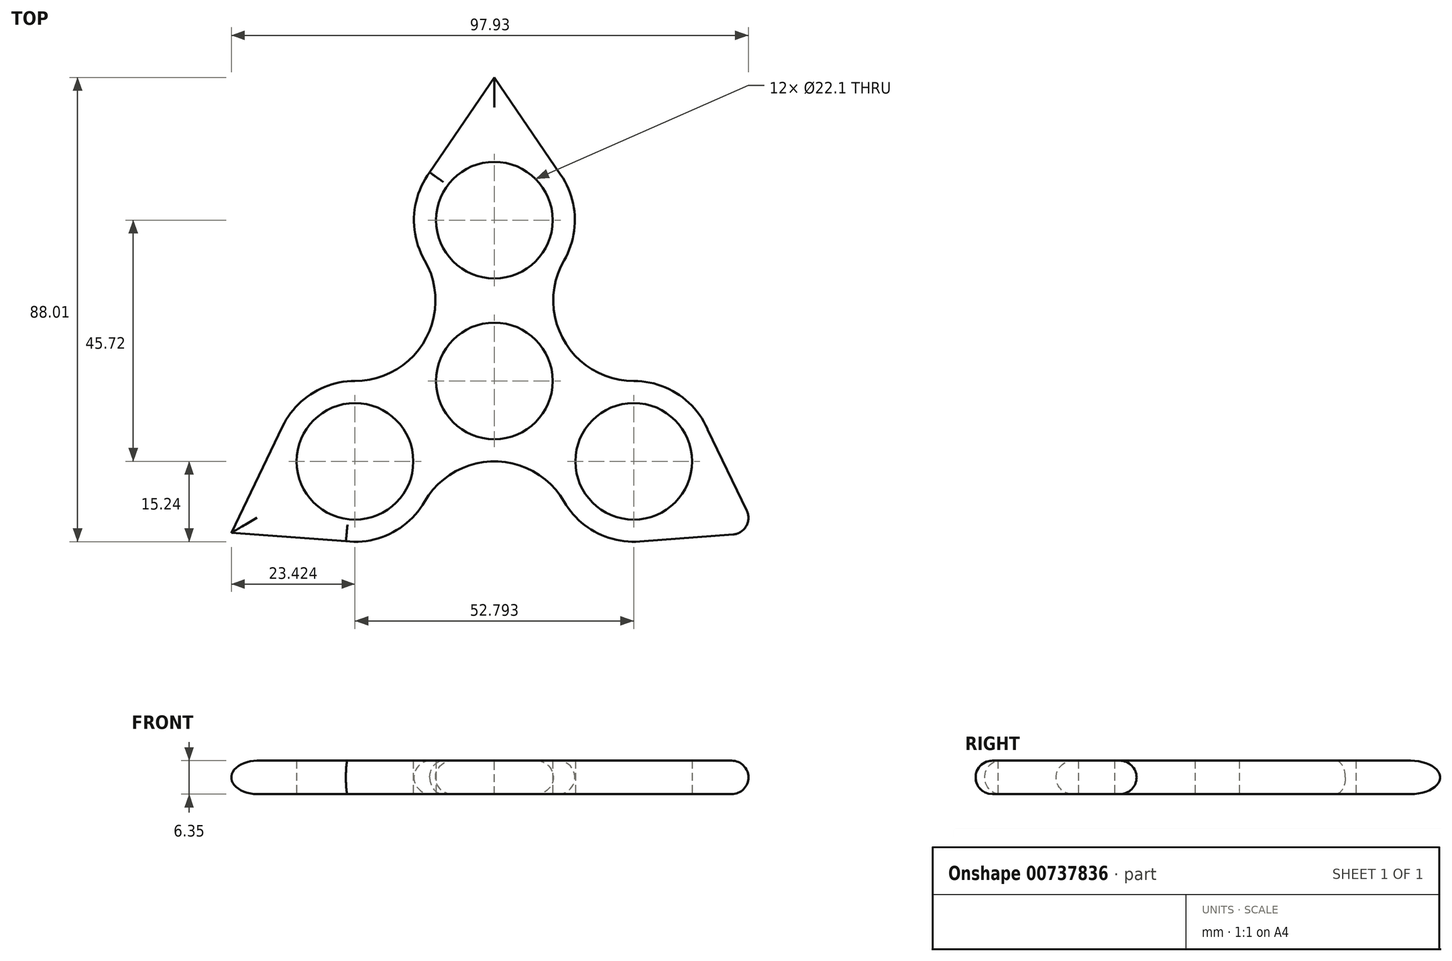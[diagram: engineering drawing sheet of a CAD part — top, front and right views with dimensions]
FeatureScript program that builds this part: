
annotation { "Feature Type Name" : "Feature", "Feature Type Description" : "" }
export const myFeature = defineFeature(function(context is Context, id is Id, definition is map)
    precondition{}
    {
        {
            var Q0;
            Q0=qCreatedBy(makeId("Top.planeOp"),FACE);
            var sketch = newSketch(context, id + "F0", { "sketchPlane" : qUnion([Q0])});
            skCircle(sketch, "E0", {"center": v(0, 0) * mm, "radius": 11.05 * mm});
            skLineSegment(sketch, "E1", {"start": v(0, 0) * mm, "end": v(0, 30.48) * mm});
            skArc(sketch, "E2", {"start": v(-12.25, 39.54) * mm, "mid": v(-15.22, 31.34) * mm, "end": v(-13.2, 22.86) * mm});
            skArc(sketch, "E3.1.0", {"start": v(-28.12, -30.38) * mm, "mid": v(-19.54, -28.85) * mm, "end": v(-13.2, -22.86) * mm});
            skArc(sketch, "E3.2.0", {"start": v(13.2, -22.86) * mm, "mid": v(19.28, -28.71) * mm, "end": v(27.54, -30.44) * mm});
            skLineSegment(sketch, "E4", {"start": v(0, 0) * mm, "end": v(-26.4, 15.24) * mm});
            skArc(sketch, "E5", {"start": v(-26.4, 0) * mm, "mid": v(-13.2, 7.62) * mm, "end": v(-13.2, 22.86) * mm});
            skArc(sketch, "E6.1.0", {"start": v(13.2, -22.86) * mm, "mid": v(0, -15.24) * mm, "end": v(-13.2, -22.86) * mm});
            skArc(sketch, "E6.2.0", {"start": v(13.2, 22.86) * mm, "mid": v(13.2, 7.62) * mm, "end": v(26.4, 0) * mm});
            skLineSegment(sketch, "E7", {"start": v(-12.25, 39.54) * mm, "end": v(0, 57.53) * mm});
            skLineSegment(sketch, "E8", {"start": v(0, 57.53) * mm, "end": v(12.6, 39.07) * mm});
            skLineSegment(sketch, "E9.1.0", {"start": v(-49.82, -28.76) * mm, "end": v(-40.13, -8.63) * mm});
            skLineSegment(sketch, "E9.2.0", {"start": v(49.82, -28.76) * mm, "end": v(27.54, -30.44) * mm});
            skLineSegment(sketch, "E10.1.0", {"start": v(-28.12, -30.38) * mm, "end": v(-49.82, -28.76) * mm});
            skLineSegment(sketch, "E10.2.0", {"start": v(40.37, -9.16) * mm, "end": v(49.82, -28.76) * mm});
            skCircle(sketch, "E11", {"center": v(0, 30.48) * mm, "radius": 11.05 * mm});
            skCircle(sketch, "E12.1.0", {"center": v(-26.4, -15.24) * mm, "radius": 11.05 * mm});
            skCircle(sketch, "E12.2.0", {"center": v(26.4, -15.24) * mm, "radius": 11.05 * mm});
            skArc(sketch, "E13.trimOffspring", {"start": v(13.2, 22.86) * mm, "mid": v(15.23, 31.05) * mm, "end": v(12.6, 39.07) * mm});
            skArc(sketch, "E14.trimOffspring", {"start": v(-26.4, 0) * mm, "mid": v(-34.5, -2.34) * mm, "end": v(-40.13, -8.63) * mm});
            skArc(sketch, "E15.trimOffspring", {"start": v(40.37, -9.16) * mm, "mid": v(34.75, -2.5) * mm, "end": v(26.4, 0) * mm});
            skSolve(sketch);
        }
        {
            var Q0;
            Q0=qSketchRegion(id+"F0",true);
            extrude(context, id + "F1", {"entities" : qUnion([Q0]), "depth" : 6.35 * mm, "offsetDistance" : 25.4 * mm});
        }
        {
            var Q0;
            Q0=makeQuery(id+"F1.opExtrude","CAP_EDGE",EDGE,{"disambiguationData":[OSD([sQuery(id+"F0.wireOp",EDGE,"E7")])],"isStart":false});
            var Q1;
            Q1=makeQuery(id+"F1.opExtrude","CAP_EDGE",EDGE,{"disambiguationData":[OSD([sQuery(id+"F0.wireOp",EDGE,"E8")])],"isStart":false});
            var Q2;
            Q2=makeQuery(id+"F1.opExtrude","CAP_EDGE",EDGE,{"disambiguationData":[OSD([sQuery(id+"F0.wireOp",EDGE,"E13.trimOffspring")])],"isStart":false});
            var Q3;
            Q3=makeQuery(id+"F1.opExtrude","CAP_EDGE",EDGE,{"disambiguationData":[OSD([sQuery(id+"F0.wireOp",EDGE,"E6.2.0")])],"isStart":false});
            var Q4;
            Q4=makeQuery(id+"F1.opExtrude","CAP_EDGE",EDGE,{"disambiguationData":[OSD([sQuery(id+"F0.wireOp",EDGE,"E15.trimOffspring")])],"isStart":false});
            var Q5;
            Q5=makeQuery(id+"F1.opExtrude","CAP_EDGE",EDGE,{"disambiguationData":[OSD([sQuery(id+"F0.wireOp",EDGE,"E10.2.0")])],"isStart":false});
            var Q6;
            Q6=makeQuery(id+"F1.opExtrude","CAP_EDGE",EDGE,{"disambiguationData":[OSD([sQuery(id+"F0.wireOp",EDGE,"E9.2.0")])],"isStart":false});
            var Q7;
            Q7=makeQuery(id+"F1.opExtrude","CAP_EDGE",EDGE,{"disambiguationData":[OSD([sQuery(id+"F0.wireOp",EDGE,"E3.2.0")])],"isStart":false});
            var Q8;
            Q8=makeQuery(id+"F1.opExtrude","CAP_EDGE",EDGE,{"disambiguationData":[OSD([sQuery(id+"F0.wireOp",EDGE,"E6.1.0")])],"isStart":false});
            var Q9;
            Q9=makeQuery(id+"F1.opExtrude","CAP_EDGE",EDGE,{"disambiguationData":[OSD([sQuery(id+"F0.wireOp",EDGE,"E3.1.0")])],"isStart":false});
            var Q10;
            Q10=makeQuery(id+"F1.opExtrude","CAP_EDGE",EDGE,{"disambiguationData":[OSD([sQuery(id+"F0.wireOp",EDGE,"E10.1.0")])],"isStart":false});
            var Q11;
            Q11=makeQuery(id+"F1.opExtrude","CAP_EDGE",EDGE,{"disambiguationData":[OSD([sQuery(id+"F0.wireOp",EDGE,"E9.1.0")])],"isStart":false});
            var Q12;
            Q12=makeQuery(id+"F1.opExtrude","CAP_EDGE",EDGE,{"disambiguationData":[OSD([sQuery(id+"F0.wireOp",EDGE,"E14.trimOffspring")])],"isStart":false});
            var Q13;
            Q13=makeQuery(id+"F1.opExtrude","CAP_EDGE",EDGE,{"disambiguationData":[OSD([sQuery(id+"F0.wireOp",EDGE,"E5")])],"isStart":false});
            var Q14;
            Q14=makeQuery(id+"F1.opExtrude","CAP_EDGE",EDGE,{"disambiguationData":[OSD([sQuery(id+"F0.wireOp",EDGE,"E2")])],"isStart":false});
            var Q15;
            Q15=makeQuery(id+"F1.opExtrude","CAP_EDGE",EDGE,{"disambiguationData":[OSD([sQuery(id+"F0.wireOp",EDGE,"E2")])],"isStart":true});
            var Q16;
            Q16=makeQuery(id+"F1.opExtrude","CAP_EDGE",EDGE,{"disambiguationData":[OSD([sQuery(id+"F0.wireOp",EDGE,"E8")])],"isStart":true});
            var Q17;
            Q17=makeQuery(id+"F1.opExtrude","CAP_EDGE",EDGE,{"disambiguationData":[OSD([sQuery(id+"F0.wireOp",EDGE,"E6.2.0")])],"isStart":true});
            var Q18;
            Q18=makeQuery(id+"F1.opExtrude","CAP_EDGE",EDGE,{"disambiguationData":[OSD([sQuery(id+"F0.wireOp",EDGE,"E9.2.0")])],"isStart":true});
            var Q19;
            Q19=makeQuery(id+"F1.opExtrude","SWEPT_FACE",FACE,{"disambiguationData":[OSD([sQuery(id+"F0.wireOp",EDGE,"E13.trimOffspring")])]});
            var Q20;
            Q20=makeQuery(id+"F1.opExtrude","SWEPT_FACE",FACE,{"disambiguationData":[OSD([sQuery(id+"F0.wireOp",EDGE,"E15.trimOffspring")])]});
            var Q21;
            Q21=makeQuery(id+"F1.opExtrude","SWEPT_FACE",FACE,{"disambiguationData":[OSD([sQuery(id+"F0.wireOp",EDGE,"E10.2.0")])]});
            var Q22;
            Q22=makeQuery(id+"F1.opExtrude","CAP_EDGE",EDGE,{"disambiguationData":[OSD([sQuery(id+"F0.wireOp",EDGE,"E5")])],"isStart":true});
            fillet(context, id + "F2", {"entities" : qUnion([Q0, Q1, Q2, Q3, Q4, Q5, Q6, Q7, Q8, Q9, Q10, Q11, Q12, Q13, Q14, Q15, Q16, Q17, Q18, Q19, Q20, Q21, Q22]), "radius" : 3.17 * mm, "tangentPropagation" : true, "allowEdgeOverflow" : false});
        }
    });
